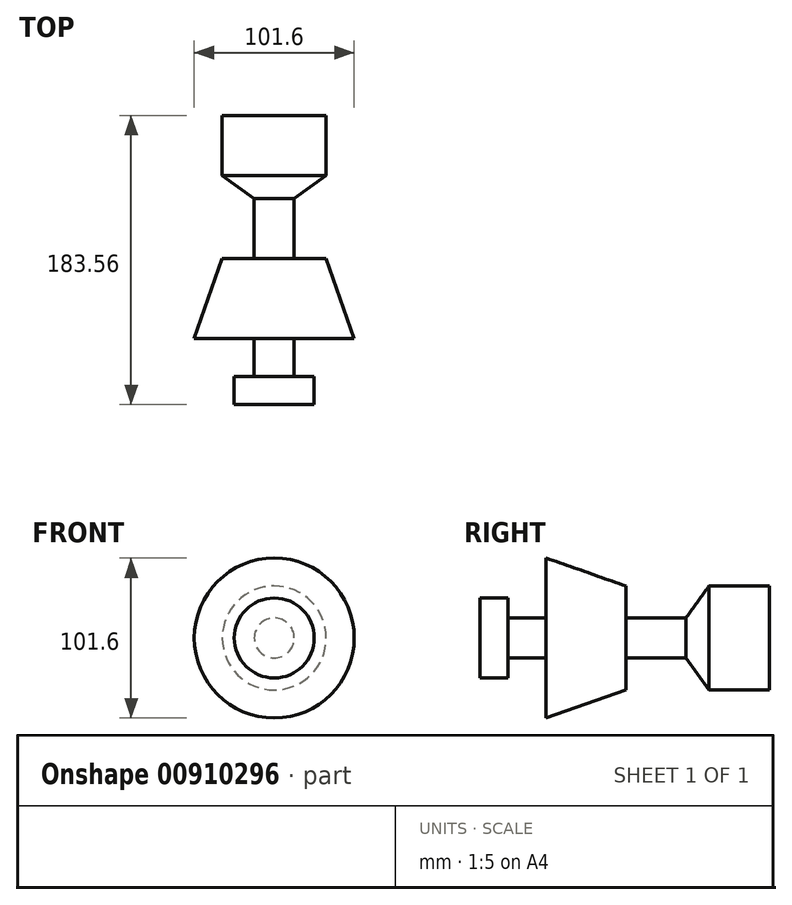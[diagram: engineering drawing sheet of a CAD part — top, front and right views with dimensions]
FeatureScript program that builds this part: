
annotation { "Feature Type Name" : "Feature", "Feature Type Description" : "" }
export const myFeature = defineFeature(function(context is Context, id is Id, definition is map)
    precondition{}
    {
        {
            var Q0;
            Q0=qCreatedBy(makeId("Right.planeOp"),FACE);
            var sketch = newSketch(context, id + "F0", { "sketchPlane" : qUnion([Q0])});
            skLineSegment(sketch, "E0", {"start": v(0, 0) * mm, "end": v(0, 25.4) * mm});
            skLineSegment(sketch, "E1", {"start": v(0, 25.4) * mm, "end": v(17.78, 25.4) * mm});
            skLineSegment(sketch, "E2", {"start": v(17.78, 25.4) * mm, "end": v(17.78, 12.7) * mm});
            skLineSegment(sketch, "E3", {"start": v(17.78, 12.7) * mm, "end": v(41.81, 12.7) * mm});
            skLineSegment(sketch, "E4", {"start": v(41.81, 12.7) * mm, "end": v(41.81, 50.8) * mm});
            skLineSegment(sketch, "E5", {"start": v(41.81, 50.8) * mm, "end": v(92.61, 33.02) * mm});
            skLineSegment(sketch, "E6", {"start": v(92.61, 33.02) * mm, "end": v(92.61, 12.7) * mm});
            skLineSegment(sketch, "E7", {"start": v(92.61, 12.7) * mm, "end": v(130.71, 12.7) * mm});
            skLineSegment(sketch, "E8", {"start": v(130.71, 12.7) * mm, "end": v(145.46, 33.02) * mm});
            skLineSegment(sketch, "E9", {"start": v(145.46, 33.02) * mm, "end": v(183.56, 33.02) * mm});
            skLineSegment(sketch, "E10", {"start": v(183.56, 33.02) * mm, "end": v(183.56, 0) * mm});
            skLineSegment(sketch, "E11", {"start": v(183.56, 0) * mm, "end": v(0, 0) * mm});
            skSolve(sketch);
        }
        {
            var Q0;
            Q0=makeQuery(id+"F0.imprint","IMPRINT",FACE,{"disambiguationData":[TD([[makeQuery(id+"F0.imprint","IMPRINT",EDGE,{"derivedFrom":sQuery(id+"F0.wireOp",EDGE,"E0")}),-1.0]])]});
            var Q1;
            Q1=sQuery(id+"F0.wireOp",EDGE,"E11");
            revolve(context, id + "F1", {"surfaceOperationType" : NewSurfaceOperationType.NEW, "entities" : qUnion([Q0]), "axis" : qUnion([Q1]), "revolveType" : RevolveType.FULL});
        }
    });
